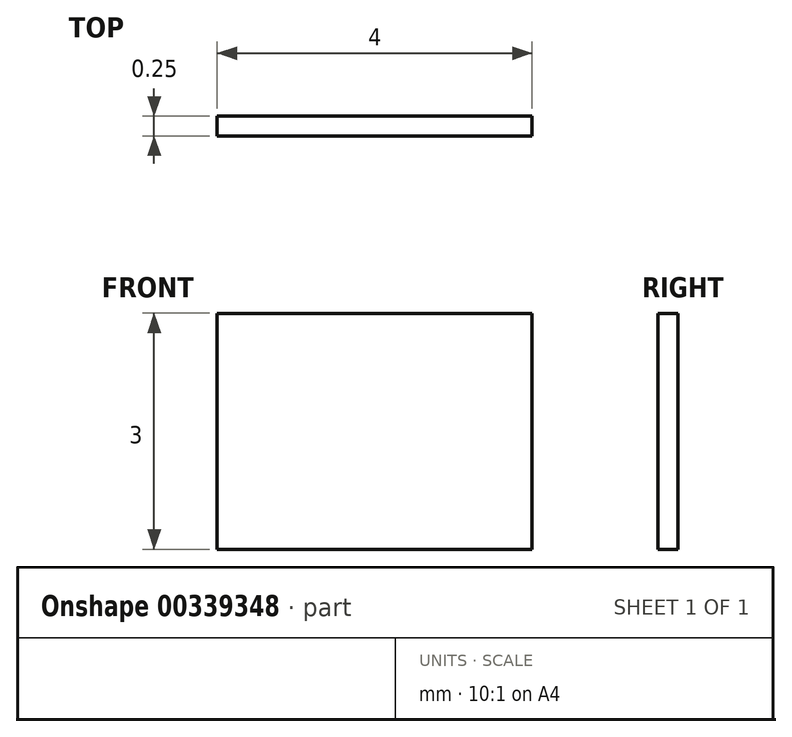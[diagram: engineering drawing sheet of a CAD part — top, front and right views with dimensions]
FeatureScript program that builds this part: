
annotation { "Feature Type Name" : "Feature", "Feature Type Description" : "" }
export const myFeature = defineFeature(function(context is Context, id is Id, definition is map)
    precondition{}
    {
        {
            var Q0;
            Q0=qCreatedBy(makeId("Front.planeOp"),FACE);
            var sketch = newSketch(context, id + "F0", { "sketchPlane" : qUnion([Q0])});
            skLineSegment(sketch, "E0", {"start": v(-27.34, -19.52) * mm, "end": v(-27.34, -22.52) * mm});
            skLineSegment(sketch, "E1", {"start": v(-27.34, -19.52) * mm, "end": v(-23.34, -19.52) * mm});
            skLineSegment(sketch, "E2", {"start": v(-23.34, -19.52) * mm, "end": v(-23.34, -22.52) * mm});
            skLineSegment(sketch, "E3", {"start": v(-23.34, -22.52) * mm, "end": v(-27.34, -22.52) * mm});
            skSolve(sketch);
        }
        {
            var Q0;
            Q0=makeQuery(id+"F0.imprint","IMPRINT",FACE,{"disambiguationData":[TD([[makeQuery(id+"F0.imprint","IMPRINT",EDGE,{"derivedFrom":sQuery(id+"F0.wireOp",EDGE,"E0")}),1.0]])]});
            extrude(context, id + "F1", {"entities" : qUnion([Q0]), "depth" : .25 * mm});
        }
    });
